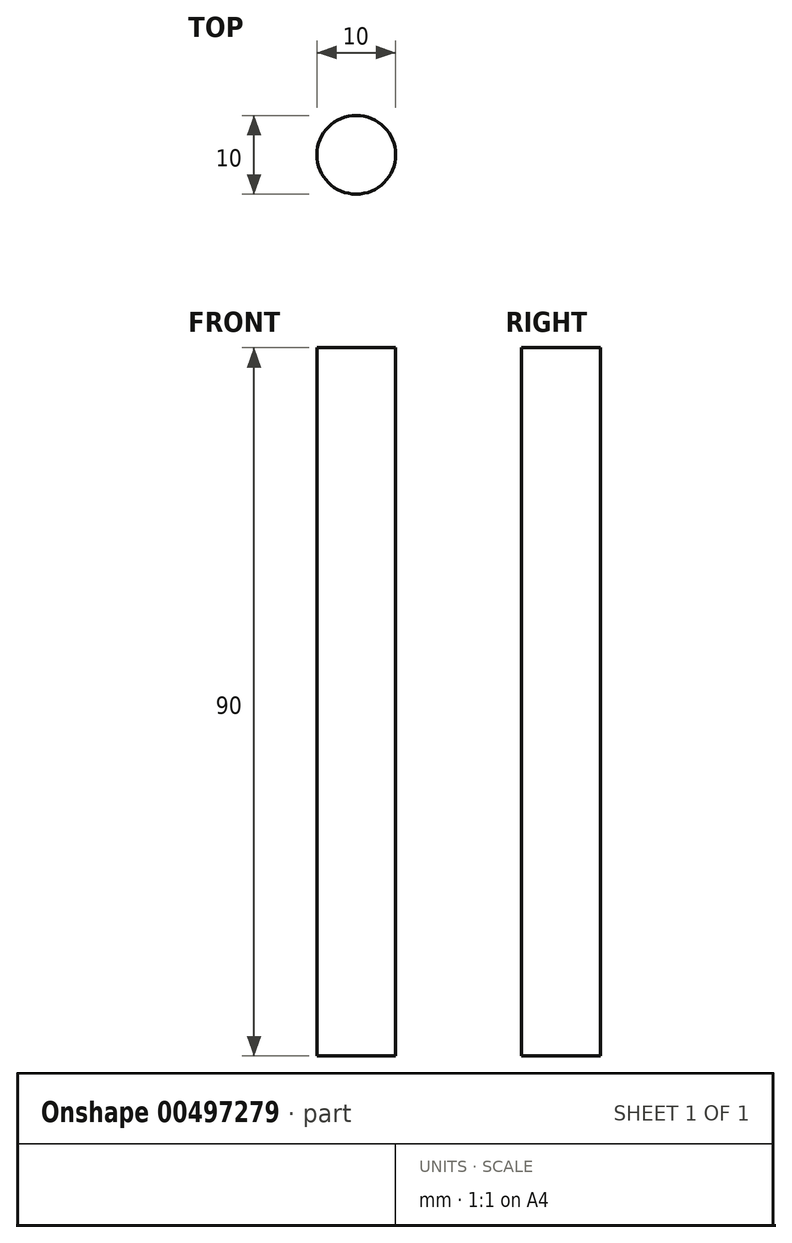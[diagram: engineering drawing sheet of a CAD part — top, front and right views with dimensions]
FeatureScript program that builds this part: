
annotation { "Feature Type Name" : "Feature", "Feature Type Description" : "" }
export const myFeature = defineFeature(function(context is Context, id is Id, definition is map)
    precondition{}
    {
        {
            var Q0;
            Q0=qCreatedBy(makeId("Top.planeOp"),FACE);
            var sketch = newSketch(context, id + "F0", { "sketchPlane" : qUnion([Q0])});
            skCircle(sketch, "E0", {"center": v(0, 0) * mm, "radius": 5 * mm});
            skSolve(sketch);
        }
        {
            var Q0;
            Q0=sQuery(id+"F0.wireOp",EDGE,"E0");
            extrude(context, id + "F1", {"bodyType" : ToolBodyType.SURFACE, "surfaceEntities" : qUnion([Q0]), "depth" : 90 * mm});
        }
        {
            var Q0;
            Q0=qCreatedBy(makeId("Top.planeOp"),FACE);
            var sketch = newSketch(context, id + "F2", { "sketchPlane" : qUnion([Q0])});
            skCircle(sketch, "E1", {"center": v(0, 0) * mm, "radius": 5 * mm});
            skSolve(sketch);
        }
        {
            var Q0;
            Q0=makeQuery(id+"F2.imprint","IMPRINT",FACE,{"disambiguationData":[TD([[makeQuery(id+"F2.imprint","IMPRINT",EDGE,{"derivedFrom":sQuery(id+"F2.wireOp",EDGE,"E1")}),1.0]])]});
            extrude(context, id + "F3", {"entities" : qUnion([Q0]), "depth" : 90 * mm});
        }
    });
